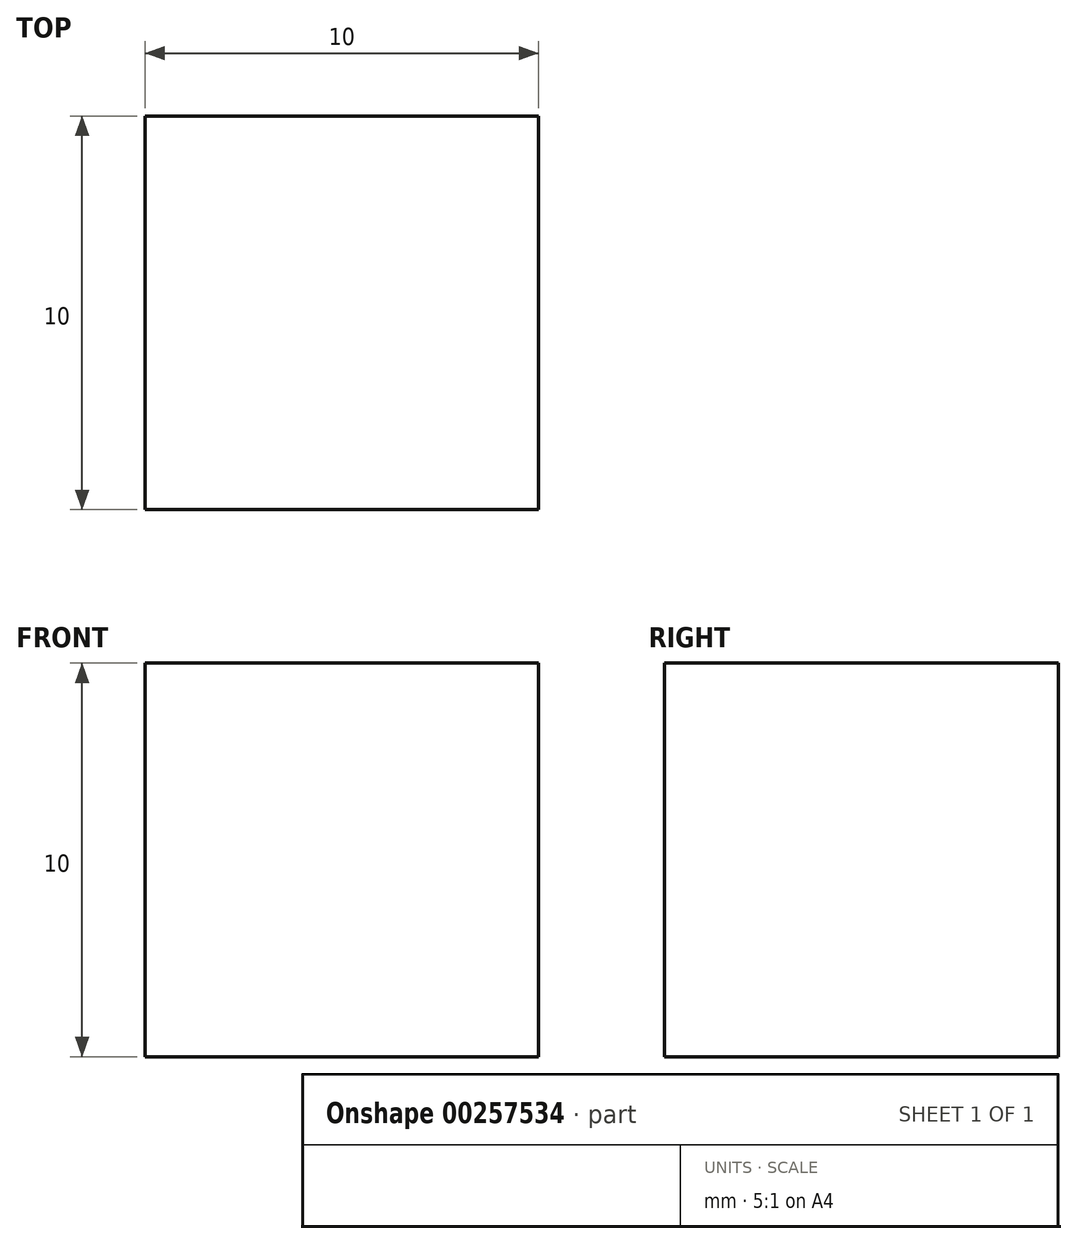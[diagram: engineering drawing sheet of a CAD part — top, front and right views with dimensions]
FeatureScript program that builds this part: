
annotation { "Feature Type Name" : "Feature", "Feature Type Description" : "" }
export const myFeature = defineFeature(function(context is Context, id is Id, definition is map)
    precondition{}
    {
        {
            var Q0;
            Q0=qCreatedBy(makeId("Top.planeOp"),FACE);
            var sketch = newSketch(context, id + "F0", { "sketchPlane" : qUnion([Q0])});
            skLineSegment(sketch, "E0.bottom", {"start": v(-5, 5) * mm, "end": v(5, 5) * mm});
            skLineSegment(sketch, "E0.top", {"start": v(-5, -5) * mm, "end": v(5, -5) * mm});
            skLineSegment(sketch, "E0.left", {"start": v(-5, 5) * mm, "end": v(-5, -5) * mm});
            skLineSegment(sketch, "E0.right", {"start": v(5, 5) * mm, "end": v(5, -5) * mm});
            skSolve(sketch);
        }
        {
            var Q0;
            Q0 = qSketchRegion(id + "F0", true);
            extrude(context, id + "F1", {"entities" : qUnion([Q0]), "depth" : 10 * mm});
        }
    });
